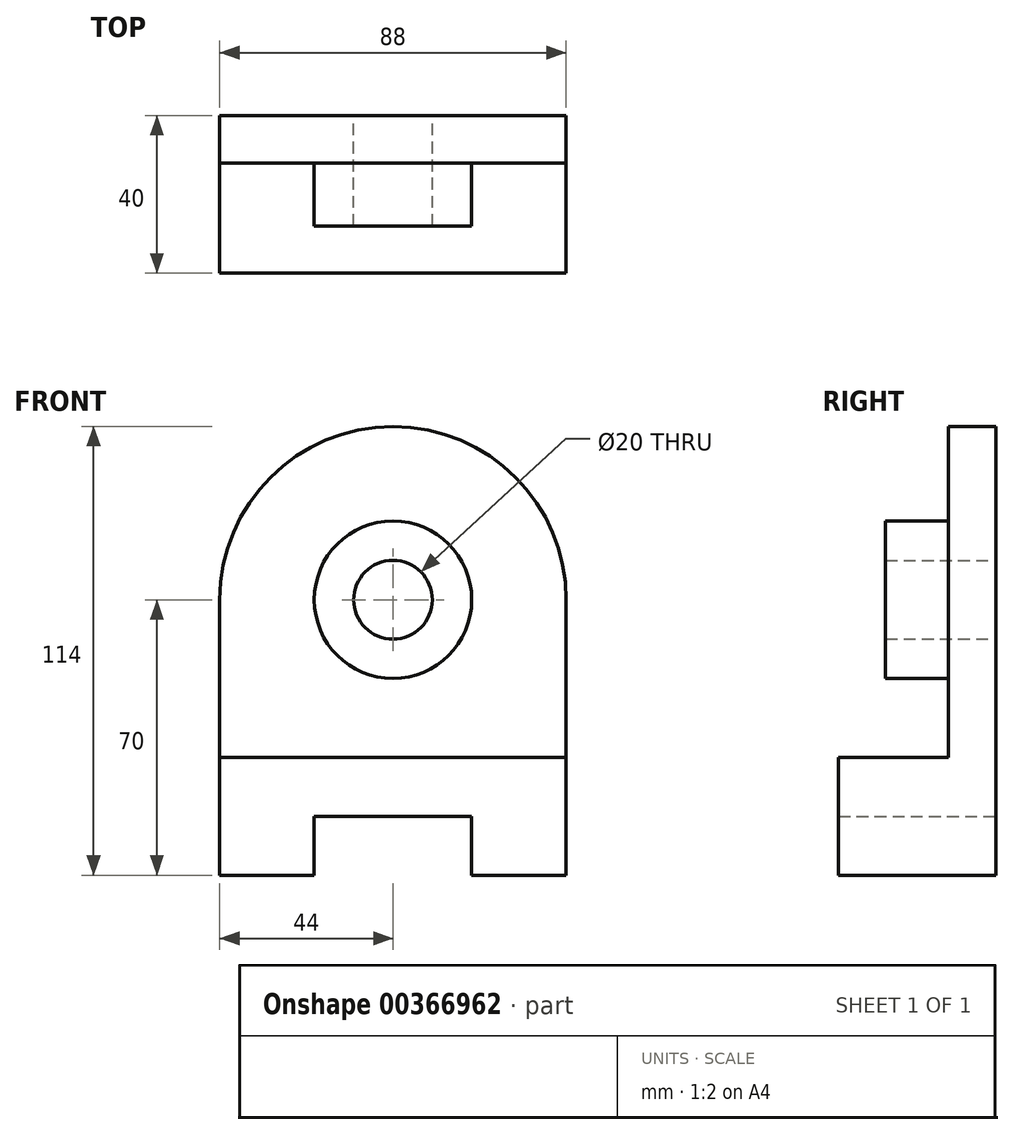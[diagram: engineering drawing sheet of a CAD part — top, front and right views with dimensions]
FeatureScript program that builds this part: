
annotation { "Feature Type Name" : "Feature", "Feature Type Description" : "" }
export const myFeature = defineFeature(function(context is Context, id is Id, definition is map)
    precondition{}
    {
        {
            var Q0;
            Q0=qCreatedBy(makeId("Front.planeOp"),FACE);
            var sketch = newSketch(context, id + "F0", { "sketchPlane" : qUnion([Q0])});
            skLineSegment(sketch, "E0", {"start": v(0, 0) * mm, "end": v(0, 30) * mm});
            skLineSegment(sketch, "E1", {"start": v(0, 30) * mm, "end": v(88, 30) * mm});
            skLineSegment(sketch, "E2", {"start": v(88, 30) * mm, "end": v(88, 0) * mm});
            skLineSegment(sketch, "E3", {"start": v(88, 0) * mm, "end": v(64, 0) * mm});
            skLineSegment(sketch, "E4", {"start": v(64, 0) * mm, "end": v(64, 15) * mm});
            skLineSegment(sketch, "E5", {"start": v(64, 15) * mm, "end": v(24, 15) * mm});
            skLineSegment(sketch, "E6", {"start": v(24, 15) * mm, "end": v(24, 0) * mm});
            skLineSegment(sketch, "E7", {"start": v(24, 0) * mm, "end": v(0, 0) * mm});
            skLineSegment(sketch, "E8", {"start": v(0, 30) * mm, "end": v(0, 70) * mm});
            skLineSegment(sketch, "E9", {"start": v(88, 70) * mm, "end": v(88, 30) * mm});
            skPoint(sketch, "E10.startSnap0", {"position": v(44, 15) * mm});
            skArc(sketch, "E11", {"start": v(88, 70) * mm, "mid": v(44, 114) * mm, "end": v(0, 70) * mm});
            skCircle(sketch, "E12", {"center": v(44, 70) * mm, "radius": 20 * mm});
            skCircle(sketch, "E13", {"center": v(44, 70) * mm, "radius": 10 * mm});
            skPoint(sketch, "E10.start.orphan", {"position": v(44, 148.5) * mm});
            skSolve(sketch);
        }
        {
            var Q0;
            Q0=makeQuery(id+"F0.imprint","IMPRINT",FACE,{"disambiguationData":[TD([[makeQuery(id+"F0.imprint","IMPRINT",EDGE,{"derivedFrom":sQuery(id+"F0.wireOp",EDGE,"E1")}),1.0]])]});
            extrude(context, id + "F1", {"entities" : qUnion([Q0]), "depth" : 12 * mm});
        }
        {
            var Q0;
            Q0=makeQuery(id+"F0.imprint","IMPRINT",FACE,{"disambiguationData":[TD([[makeQuery(id+"F0.imprint","IMPRINT",EDGE,{"derivedFrom":sQuery(id+"F0.wireOp",EDGE,"E0")}),-1.0]])]});
            extrude(context, id + "F2", {"entities" : qUnion([Q0]), "operationType" : NewBodyOperationType.ADD, "depth" : 40 * mm});
        }
        {
            var Q0;
            Q0=makeQuery(id+"F0.imprint","IMPRINT",FACE,{"disambiguationData":[TD([[makeQuery(id+"F0.imprint","IMPRINT",EDGE,{"derivedFrom":sQuery(id+"F0.wireOp",EDGE,"E12")}),1.0]])]});
            extrude(context, id + "F3", {"entities" : qUnion([Q0]), "operationType" : NewBodyOperationType.ADD, "depth" : 28 * mm});
        }
        {
            var Q0;
            Q0=makeQuery(id+"F0.imprint","IMPRINT",FACE,{"disambiguationData":[TD([[makeQuery(id+"F0.imprint","IMPRINT",EDGE,{"derivedFrom":sQuery(id+"F0.wireOp",EDGE,"E13")}),1.0]])]});
            extrude(context, id + "F4", {"entities" : qUnion([Q0]), "operationType" : NewBodyOperationType.REMOVE, "oppositeDirection" : true, "depth" : 25 * mm});
        }
    });
